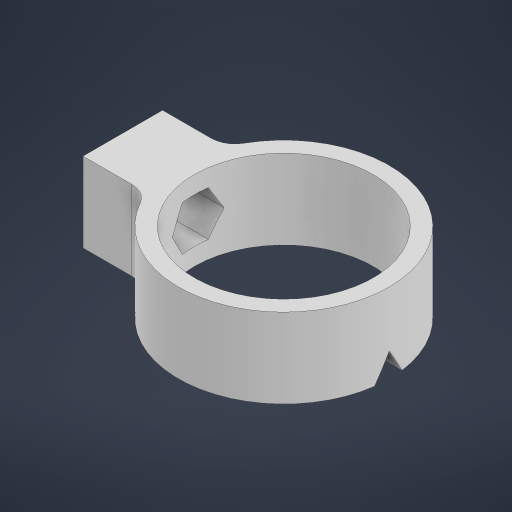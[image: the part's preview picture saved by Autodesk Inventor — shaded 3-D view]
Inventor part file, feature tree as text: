
AUTODESK INVENTOR PART (.ipt)
format: ipt  version: 2023 (Build 270158000, 158)  size: 236,544 bytes
history: native  units: mm
features: extrude x5, sketch x4, plane x2, fillet x1, projected_geometry x1
ambient origin geometry x8: Origin, YZ Plane, XZ Plane, XY Plane, X Axis, Y Axis, Z Axis, Center Point
bodies: Solid1 (feature_tree)
feature tree (13):
  extrude  "Extrusion1"  Depth=2.0mm
  plane  "Work Plane1"
  extrude  "Extrusion2"  Depth=10.0mm
  plane  "Work Plane2"
  extrude  "Extrusion4"  TaperAngle=60.0deg  [1 undecoded]
  sketch  "Sketch7"  dims[d8=3.0mm d9=12.25mm d10=0.0mm d14=-20.25mm d16=0.2mm d18=10.25mm d19=0.0mm d20=6.5mm d21=60.0mm d23=360.0deg d25=3.6mm d26=10.0mm d27=0.0mm d28=5.0mm d29=0.0mm d30=3.0mm d31=10.0mm]
  extrude  "Extrusion5"  Depth=10.0mm TaperAngle=0.0deg
  extrude  "Extrusion6"  [1 undecoded]
  fillet  "Fillet1"  Radius=0.2mm
  sketch  "Sketch1"  dims[d0=22.5mm d1=2.0mm]
  sketch  "Sketch2"  dims[d2=10.0mm d3=0.0mm d4=15.5mm]
  projected_geometry  "Projected Loop1"
  sketch  "Sketch5"  dims[d5=60.0deg d7=60.0deg]
note: 2 required parameter values undecoded (feature->parameter linkage not recoverable at this tier; creation-order binding heuristic only, values carry confidence <= 0.55)
